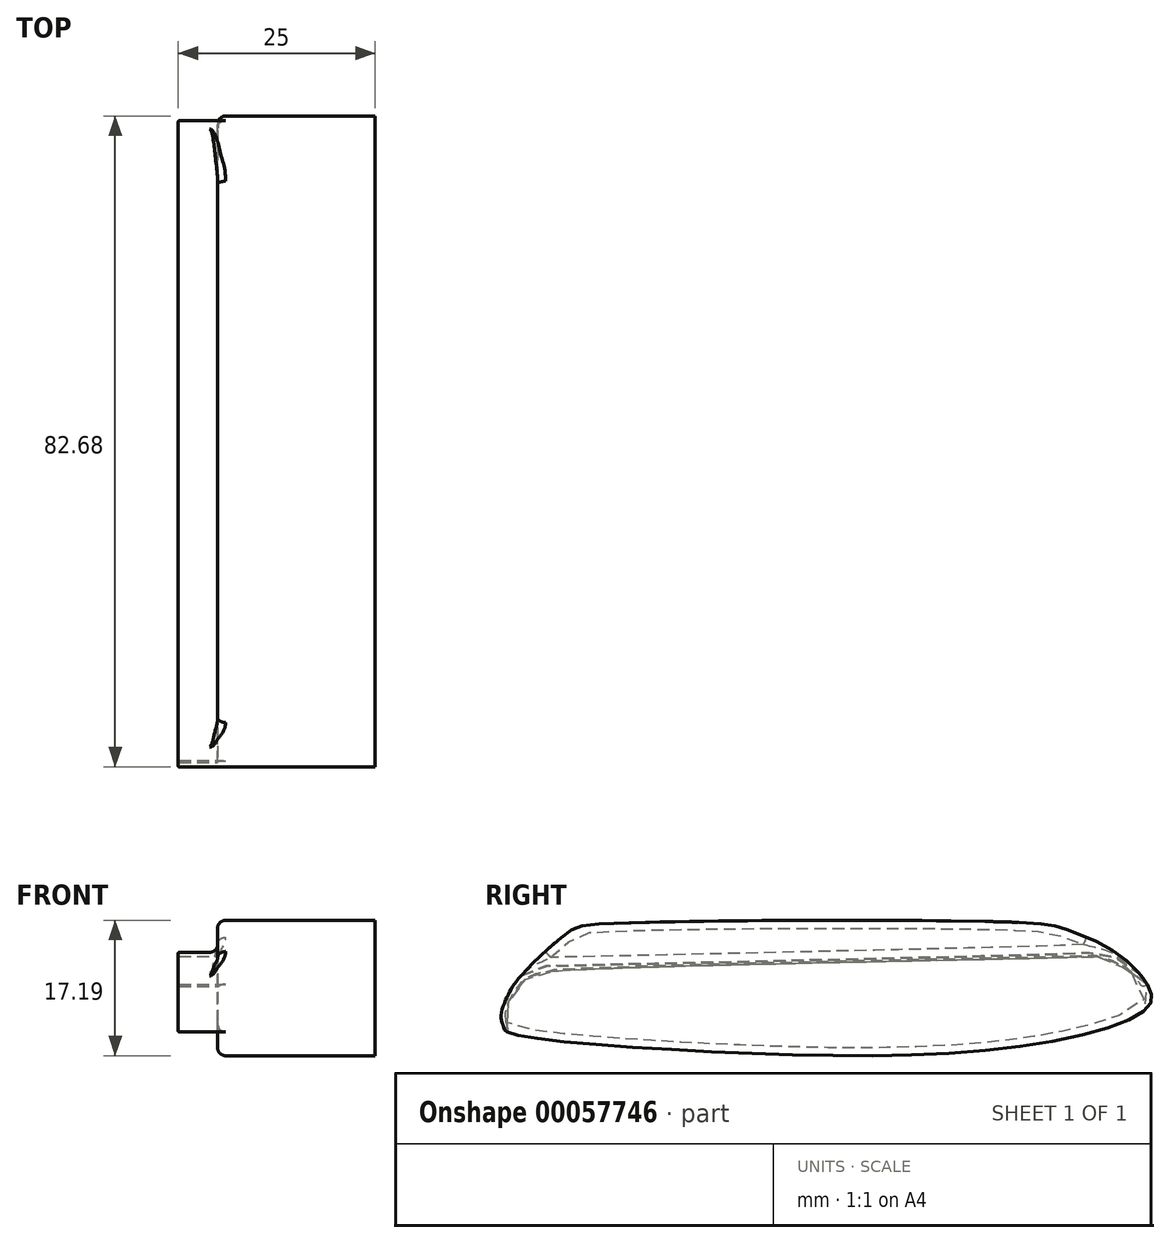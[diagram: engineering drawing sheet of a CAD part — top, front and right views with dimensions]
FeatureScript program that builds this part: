
annotation { "Feature Type Name" : "Feature", "Feature Type Description" : "" }
export const myFeature = defineFeature(function(context is Context, id is Id, definition is map)
    precondition{}
    {
        {
            var Q0;
            Q0=qCreatedBy(makeId("Right.planeOp"),FACE);
            var sketch = newSketch(context, id + "F0", { "sketchPlane" : qUnion([Q0])});
            skCircle(sketch, "E0", {"center": v(-28.96, -3.17) * mm, "radius": 5 * mm});
            skCircle(sketch, "E1", {"center": v(-2.58, -4.3) * mm, "radius": 5 * mm});
            skCircle(sketch, "E2", {"center": v(39.7, -1.22) * mm, "radius": 5 * mm});
            skCircle(sketch, "E3", {"center": v(-18.18, -4.4) * mm, "radius": 5 * mm});
            skCircle(sketch, "E4", {"center": v(-10.3, -4.22) * mm, "radius": 5 * mm});
            skCircle(sketch, "E5", {"center": v(5.45, -4.3) * mm, "radius": 5 * mm});
            skCircle(sketch, "E6", {"center": v(13.65, -4.38) * mm, "radius": 5 * mm});
            skCircle(sketch, "E7", {"center": v(21.76, -4.3) * mm, "radius": 5 * mm});
            skCircle(sketch, "E8", {"center": v(30, -3.33) * mm, "radius": 5 * mm});
            skCircle(sketch, "E9", {"center": v(-23.68, -3.72) * mm, "radius": 5 * mm});
            skFitSpline(sketch, "E10", {"points": [v(-24.17, -9.89) * mm, v(-31.03, -7.92) * mm, v(-32.53, -6.92) * mm, v(-33.27, -6.1) * mm, v(-33.97, -4.52) * mm, v(-34.12, -2.96) * mm, v(-33.94, -1.56) * mm, v(-32.9, 0.38) * mm, v(-30.87, 1.84) * mm, v(-29.21, 2.25) * mm, v(-21.63, 2.4) * mm, v(-13.26, 2.7) * mm, v(0.23, 3.13) * mm, v(12.27, 3.48) * mm, v(21.47, 3.78) * mm, v(33.09, 4.1) * mm, v(40.9, 4.3) * mm, v(43.62, 3.13) * mm, v(44.92, 1.76) * mm, v(45.6, 0.14) * mm, v(45.77, -1.5) * mm, v(45.48, -3) * mm, v(44.3, -5.04) * mm, v(42.31, -6.55) * mm, v(39.76, -7.29) * mm, v(33.79, -9.01) * mm, v(30.2, -9.88) * mm, v(27.4, -9.9) * mm, v(15.87, -9.91) * mm, v(8.9, -9.95) * mm, v(0.58, -9.94) * mm, v(-6.07, -9.92) * mm, v(-23.25, -9.9) * mm, v(-24, -9.9) * mm, v(-24.17, -9.89) * mm]});
            skFitSpline(sketch, "E11", {"points": [v(36.24, 2.39) * mm, v(-29.3, 0.64) * mm, v(-31.26, -0.5) * mm, v(-31.92, -1.76) * mm, v(-32.1, -3.51) * mm, v(-31.2, -5.66) * mm, v(-24.35, -8.14) * mm, v(-14.07, -8.25) * mm, v(26.48, -8.3) * mm, v(38.18, -5.98) * mm], "startDerivative": vector(-329.05, -3.13) * mm, "endDerivative": vector(74.4, 23.16) * mm});
            skSolve(sketch);
        }
        {
            var Q0;
            Q0=qCreatedBy(makeId("Right.planeOp"),FACE);
            var sketch = newSketch(context, id + "F1", { "sketchPlane" : qUnion([Q0])});
            skFitSpline(sketch, "E12", {"points": [v(36.5, 8.31) * mm, v(42.87, 5.28) * mm, v(46.9, 0.9) * mm, v(46.83, -1.43) * mm, v(31.26, -6.4) * mm, v(-11.57, -7.01) * mm, v(-34.69, -4.66) * mm, v(-35.08, -4.1) * mm, v(-35.44, -2.66) * mm, v(-34.57, 0) * mm, v(-32.87, 2.52) * mm, v(-27.16, 7.83) * mm, v(-23, 9.05) * mm, v(30.36, 9.25) * mm, v(36.5, 8.31) * mm]});
            skFitSpline(sketch, "E13", {"points": [v(-34.68, -4.66) * mm, v(-34.8, -3.51) * mm, v(-34.69, -1.45) * mm, v(-33.15, 1.3) * mm, v(-31.66, 2.48) * mm, v(-28.8, 3.1) * mm, v(36.47, 4.84) * mm, v(38.94, 4.94) * mm, v(41.08, 4.8) * mm, v(42.63, 4.23) * mm, v(45.1, 2.3) * mm, v(46.13, 1.12) * mm, v(46.64, 1.4) * mm], "startDerivative": vector(12.96, 14.65) * mm, "endDerivative": vector(18.3, 7.73) * mm});
            skFitSpline(sketch, "E14", {"points": [v(-32.87, 2.52) * mm, v(-31.16, 3.66) * mm, v(-28.85, 3.82) * mm, v(36.43, 5.35) * mm, v(38.82, 5.46) * mm, v(41.16, 5.35) * mm, v(42.86, 4.79) * mm, v(45.56, 2.87) * mm], "startDerivative": vector(36.83, 28.97) * mm, "endDerivative": vector(25.96, -24.19) * mm});
            skSolve(sketch);
        }
        {
            var Q0;
            {var subQ0=sQuery(id+"F1.wireOp",EDGE,"E14");Q0=makeQuery(id+"F1.imprint","IMPRINT",FACE,{"disambiguationData":[TD([[makeQuery(id+"F1.imprint","IMPRINT",EDGE,{"derivedFrom":subQ0}),1.0]])]});}
            var Q1;
            {var subQ0=sQuery(id+"F1.wireOp",EDGE,"E13");Q1=makeQuery(id+"F1.imprint","IMPRINT",FACE,{"disambiguationData":[TD([[makeQuery(id+"F1.imprint","IMPRINT",EDGE,{"derivedFrom":subQ0}),1.0]])]});}
            var Q2;
            {var subQ0=sQuery(id+"F1.wireOp",EDGE,"E13");Q2=makeQuery(id+"F1.imprint","IMPRINT",FACE,{"disambiguationData":[TD([[makeQuery(id+"F1.imprint","IMPRINT",EDGE,{"derivedFrom":subQ0}),-1.0]])]});}
            extrude(context, id + "F2", {"entities" : qUnion([Q0, Q1, Q2]), "depth" : 20 * mm});
        }
        {
            var Q0;
            {var subQ0=sQuery(id+"F1.wireOp",EDGE,"E13");Q0=makeQuery(id+"F1.imprint","IMPRINT",FACE,{"disambiguationData":[TD([[makeQuery(id+"F1.imprint","IMPRINT",EDGE,{"derivedFrom":subQ0}),1.0]])]});}
            extrude(context, id + "F3", {"entities" : qUnion([Q0]), "operationType" : NewBodyOperationType.ADD, "oppositeDirection" : true, "depth" : 5 * mm});
        }
        {
            var Q0;
            Q0=makeQuery(id+"F3.opExtrude","CAP_FACE",FACE,{"disambiguationData":[OSD([sQuery(id+"F1.wireOp",EDGE,"E12"),sQuery(id+"F1.wireOp",EDGE,"E13"),sQuery(id+"F1.wireOp",EDGE,"E14")])],"isStart":false});
            fillet(context, id + "F4", {"entities" : qUnion([Q0]), "radius" : .1 * mm, "tangentPropagation" : true, "allowEdgeOverflow" : false});
        }
        {
            var Q0;
            Q0=makeQuery(id+"F3.opExtrude","CAP_EDGE",EDGE,{"disambiguationData":[OSD([sQuery(id+"F1.wireOp",EDGE,"E14")])],"isStart":true});
            fillet(context, id + "F5", {"entities" : qUnion([Q0]), "radius" : 1 * mm, "tangentPropagation" : true, "allowEdgeOverflow" : false});
        }
        {
            var Q0;
            {var subQ1=sQuery(id+"F1.wireOp",EDGE,"E12");var subQ2=sQuery(id+"F1.wireOp",EDGE,"E14");Q0=makeQuery(id+"F3.boolean.opBoolean","SPLIT",EDGE,{"disambiguationData":[TD([makeQuery(id+"F3.opExtrude","SWEPT_FACE",FACE,{"disambiguationData":[OSD([subQ2])]})])],"derivedFrom":makeQuery(id+"F2.opExtrude","CAP_EDGE",EDGE,{"disambiguationData":[OSD([subQ1])],"isStart":true})});}
            fillet(context, id + "F6", {"entities" : qUnion([Q0]), "radius" : 1 * mm, "tangentPropagation" : true, "allowEdgeOverflow" : false});
        }
    });
